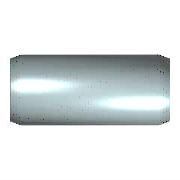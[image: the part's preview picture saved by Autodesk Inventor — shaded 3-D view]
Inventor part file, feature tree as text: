
AUTODESK INVENTOR PART (.ipt)
format: ipt  version: 2023.3 (Build 273359000, 359)  size: 113,664 bytes
history: native  units: mm (DEFAULTED — no unit token found)
features: extrude x1, chamfer x1, sketch x1
ambient origin geometry x8: Origin, YZ Plane, XZ Plane, XY Plane, X Axis, Y Axis, Z Axis, Center Point
bodies: Solid1 (feature_tree)
feature tree (3):
  extrude  "Körper"  Depth=14.0mm
  chamfer  "Skizze2"  [1 undecoded]
  sketch  "Skizze"  dims[d1=1.5mm d2=14.0mm d3=0.0mm d4=0.3mm d5=15.0deg d8=0.3mm d9=15.0deg d11=0.3mm d12=0.3mm d13=0.0mm d15=0.0mm d16=0.0mm]
note: 1 required parameter value undecoded (feature->parameter linkage not recoverable at this tier; creation-order binding heuristic only, values carry confidence <= 0.55)
